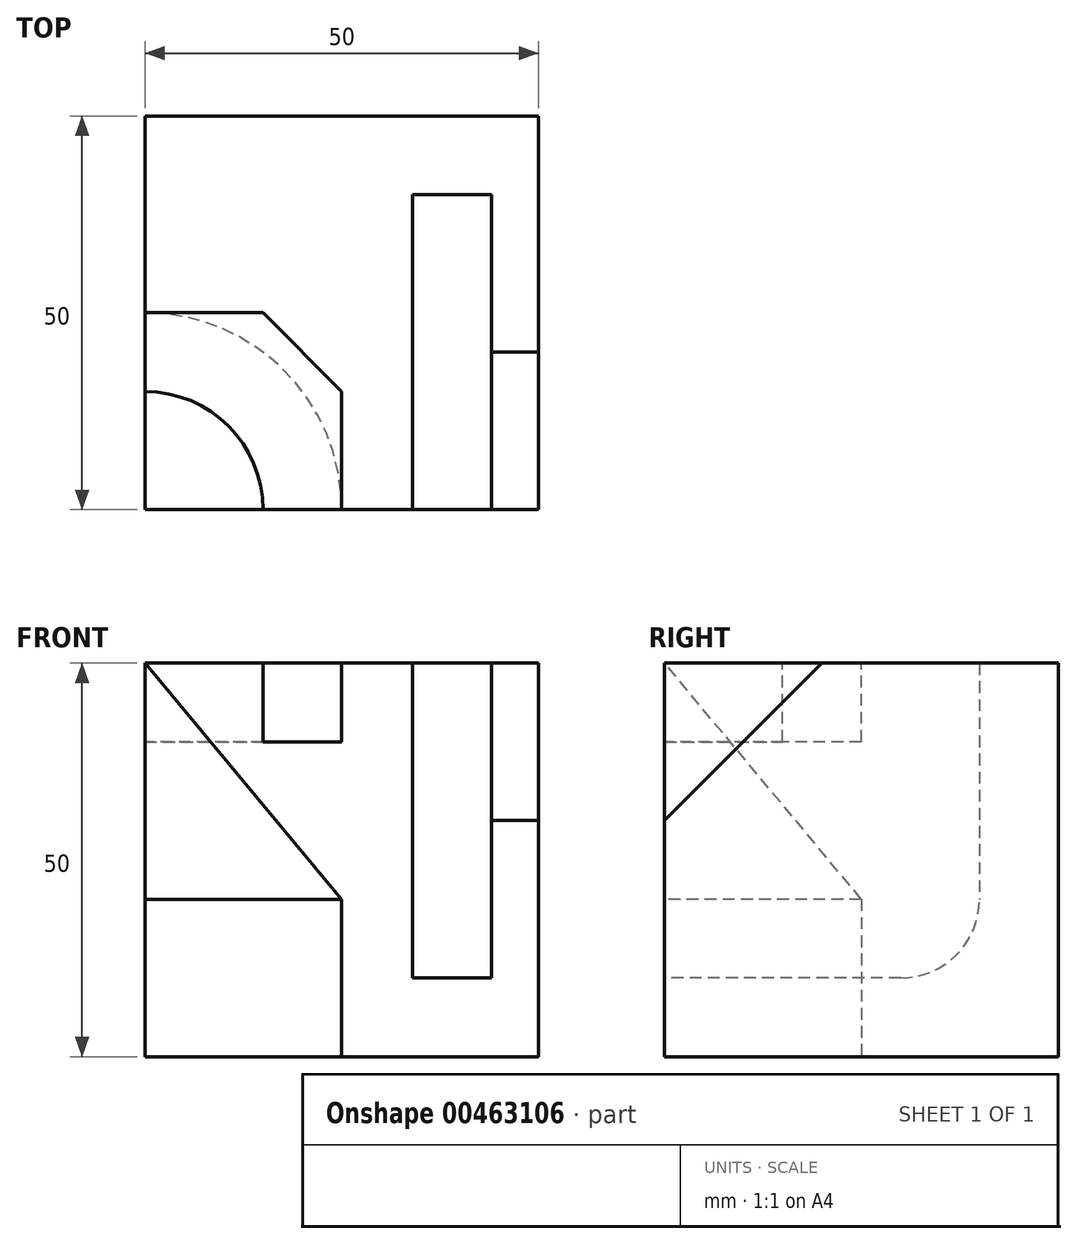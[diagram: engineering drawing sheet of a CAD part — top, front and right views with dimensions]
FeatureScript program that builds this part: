
annotation { "Feature Type Name" : "Feature", "Feature Type Description" : "" }
export const myFeature = defineFeature(function(context is Context, id is Id, definition is map)
    precondition{}
    {
        {
            var Q0;
            Q0=qCreatedBy(makeId("Top.planeOp"),FACE);
            var sketch = newSketch(context, id + "F0", { "sketchPlane" : qUnion([Q0])});
            skLineSegment(sketch, "E0.bottom", {"start": v(0, 0) * mm, "end": v(50, 0) * mm});
            skLineSegment(sketch, "E0.top", {"start": v(0, -50) * mm, "end": v(50, -50) * mm});
            skLineSegment(sketch, "E0.left", {"start": v(0, 0) * mm, "end": v(0, -50) * mm});
            skLineSegment(sketch, "E0.right", {"start": v(50, 0) * mm, "end": v(50, -50) * mm});
            skSolve(sketch);
        }
        {
            var Q0;
            Q0 = qSketchRegion(id + "F0", true);
            extrude(context, id + "F1", {"entities" : qUnion([Q0]), "depth" : 50 * mm});
        }
        {
            var Q0;
            Q0=makeQuery(id+"F1.opExtrude","SWEPT_FACE",FACE,{"disambiguationData":[OSD([sQuery(id+"F0.wireOp",EDGE,"E0.right")])]});
            var sketch = newSketch(context, id + "F2", { "sketchPlane" : qUnion([Q0])});
            skLineSegment(sketch, "E1", {"start": v(-50, 50) * mm, "end": v(-50, 30) * mm});
            skLineSegment(sketch, "E2", {"start": v(-50, 30) * mm, "end": v(-30, 50) * mm});
            skLineSegment(sketch, "E3", {"start": v(-30, 50) * mm, "end": v(-50, 50) * mm});
            skSolve(sketch);
        }
        {
            var Q0;
            Q0 = qSketchRegion(id + "F2", true);
            extrude(context, id + "F3", {"entities" : qUnion([Q0]), "operationType" : NewBodyOperationType.REMOVE, "oppositeDirection" : true, "depth" : 6 * mm});
        }
        {
            var Q0;
            Q0=makeQuery(id+"F1.opExtrude","SWEPT_FACE",FACE,{"disambiguationData":[OSD([sQuery(id+"F0.wireOp",EDGE,"E0.top")])]});
            var sketch = newSketch(context, id + "F4", { "sketchPlane" : qUnion([Q0])});
            skLineSegment(sketch, "E4.bottom", {"start": v(44, 50) * mm, "end": v(34, 50) * mm});
            skLineSegment(sketch, "E4.top", {"start": v(44, 10) * mm, "end": v(34, 10) * mm});
            skLineSegment(sketch, "E4.left", {"start": v(44, 50) * mm, "end": v(44, 10) * mm});
            skLineSegment(sketch, "E4.right", {"start": v(34, 50) * mm, "end": v(34, 10) * mm});
            skSolve(sketch);
        }
        {
            var Q0;
            Q0 = qSketchRegion(id + "F4", true);
            extrude(context, id + "F5", {"entities" : qUnion([Q0]), "operationType" : NewBodyOperationType.REMOVE, "oppositeDirection" : true, "depth" : 40 * mm});
        }
        {
            var Q0;
            Q0=makeQuery(id+"F5.boolean.opBoolean","COPY",EDGE,{"derivedFrom":makeQuery(id+"F5.opExtrude","CAP_EDGE",EDGE,{"disambiguationData":[OSD([sQuery(id+"F4.wireOp",EDGE,"E4.top")])],"isStart":false})});
            fillet(context, id + "F6", {"entities" : qUnion([Q0]), "radius" : 10 * mm, "tangentPropagation" : true, "allowEdgeOverflow" : false});
        }
        {
            var Q0;
            Q0=makeQuery(id+"F1.opExtrude","CAP_FACE",FACE,{"disambiguationData":[OSD([sQuery(id+"F0.wireOp",EDGE,"E0.bottom"),sQuery(id+"F0.wireOp",EDGE,"E0.top"),sQuery(id+"F0.wireOp",EDGE,"E0.left"),sQuery(id+"F0.wireOp",EDGE,"E0.right")])],"isStart":false});
            var sketch = newSketch(context, id + "F7", { "sketchPlane" : qUnion([Q0])});
            skLineSegment(sketch, "E5", {"start": v(0, -50) * mm, "end": v(0, -35) * mm});
            skLineSegment(sketch, "E6", {"start": v(0, -50) * mm, "end": v(15, -50) * mm});
            skArc(sketch, "E7", {"start": v(15, -50) * mm, "mid": v(10.6, -39.4) * mm, "end": v(0, -35) * mm});
            skLineSegment(sketch, "E8", {"start": v(0, -50) * mm, "end": v(25, -50) * mm});
            skLineSegment(sketch, "E9", {"start": v(0, -50) * mm, "end": v(0, -25) * mm});
            skLineSegment(sketch, "E10", {"start": v(0, -25) * mm, "end": v(25, -25) * mm});
            skLineSegment(sketch, "E11", {"start": v(25, -25) * mm, "end": v(25, -50) * mm});
            skSolve(sketch);
        }
        {
            var Q0;
            {var subQ0=sQuery(id+"F7.wireOp",EDGE,"E7");Q0=makeQuery(id+"F7.imprint","IMPRINT",FACE,{"disambiguationData":[TD([[makeQuery(id+"F7.imprint","IMPRINT",EDGE,{"derivedFrom":subQ0}),-1.0]])]});}
            extrude(context, id + "F8", {"entities" : qUnion([Q0]), "operationType" : NewBodyOperationType.REMOVE, "oppositeDirection" : true, "depth" : 10 * mm});
        }
        {
            var Q0;
            Q0=makeQuery(id+"F8.boolean.opBoolean","COPY",EDGE,{"derivedFrom":makeQuery(id+"F8.opExtrude","SWEPT_EDGE",EDGE,{"disambiguationData":[OSD([sQuery(id+"F7.wireOp",EDGE,"E10"),sQuery(id+"F7.wireOp",EDGE,"E11")])]})});
            chamfer(context, id + "F9", {"entities" : qUnion([Q0]), "width" : 10 * mm, "tangentPropagation" : true});
        }
        {
            var Q0;
            Q0=makeQuery(id+"F1.opExtrude","CAP_FACE",FACE,{"disambiguationData":[OSD([sQuery(id+"F0.wireOp",EDGE,"E0.bottom"),sQuery(id+"F0.wireOp",EDGE,"E0.top"),sQuery(id+"F0.wireOp",EDGE,"E0.left"),sQuery(id+"F0.wireOp",EDGE,"E0.right")])],"isStart":true});
            var sketch = newSketch(context, id + "F10", { "sketchPlane" : qUnion([Q0])});
            skLineSegment(sketch, "E12.bottom", {"start": v(0, 50) * mm, "end": v(25, 50) * mm});
            skLineSegment(sketch, "E12.left", {"start": v(0, 50) * mm, "end": v(0, 25) * mm});
            skArc(sketch, "E13", {"start": v(0, 25) * mm, "mid": v(17.68, 32.32) * mm, "end": v(25, 50) * mm});
            skSolve(sketch);
        }
        {
            var Q0;
            Q0 = qSketchRegion(id + "F10", true);
            var Q1;
            {var subQ0=sQuery(id+"F10.wireOp",EDGE,"xQvsmV3d-aVNt-8Ns8-ic0F-kzWMVpgDuq8N");Q1=makeQuery(id+"F10.imprint","IMPRINT",FACE,{"disambiguationData":[TD([[makeQuery(id+"F10.imprint","IMPRINT",EDGE,{"derivedFrom":subQ0}),1.0]])]});}
            extrude(context, id + "F11", {"entities" : qUnion([Q0, Q1]), "operationType" : NewBodyOperationType.REMOVE, "oppositeDirection" : true, "depth" : 20 * mm});
        }
        {
            var Q0;
            Q0 = qSketchRegion(id + "F10", true);
            extrude(context, id + "F12", {"entities" : qUnion([Q0]), "operationType" : NewBodyOperationType.REMOVE, "oppositeDirection" : true, "depth" : 20 * mm});
        }
        {
            var Q0;
            Q0=makeQuery(id+"F1.opExtrude","SWEPT_FACE",FACE,{"disambiguationData":[OSD([sQuery(id+"F0.wireOp",EDGE,"E0.top")])]});
            var sketch = newSketch(context, id + "F13", { "sketchPlane" : qUnion([Q0])});
            skLineSegment(sketch, "E14", {"start": v(0, 50) * mm, "end": v(25, 20) * mm});
            skSolve(sketch);
        }
        {
            var Q1;
            Q1=makeQuery(id+"F11.boolean.opBoolean","COPY",FACE,{"derivedFrom":makeQuery(id+"F11.opExtrude","CAP_FACE",FACE,{"disambiguationData":[OSD([sQuery(id+"F10.wireOp",EDGE,"E12.bottom"),sQuery(id+"F10.wireOp",EDGE,"E12.left"),sQuery(id+"F10.wireOp",EDGE,"E13")])],"isStart":false})});
            var Q2;
            Q2=sQuery(id+"F13.wireOp",VERTEX,"E14.start");
            loft(context, id + "F14", {"operationType" : NewBodyOperationType.REMOVE, "sheetProfilesArray" : [{ "sheetProfileEntities" : qUnion([Q1]) }, { "sheetProfileEntities" : qUnion([Q2]) }]});
        }
    });
